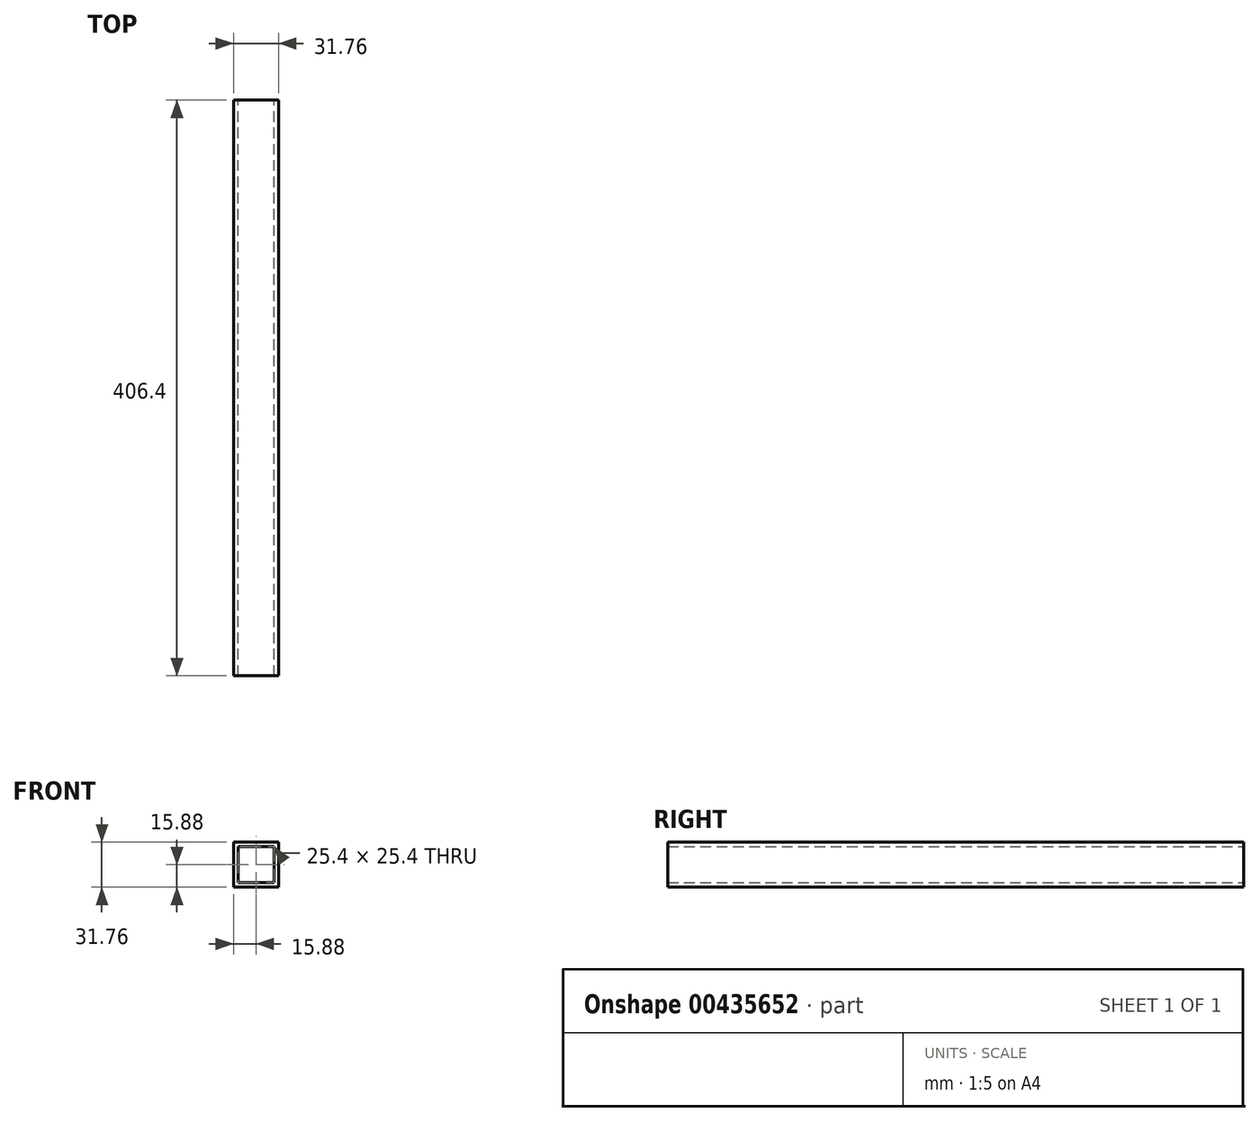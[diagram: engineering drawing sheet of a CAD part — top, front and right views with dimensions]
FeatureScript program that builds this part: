
annotation { "Feature Type Name" : "Feature", "Feature Type Description" : "" }
export const myFeature = defineFeature(function(context is Context, id is Id, definition is map)
    precondition{}
    {
        {
            var Q0;
            Q0=qCreatedBy(makeId("Front.planeOp"),FACE);
            var sketch = newSketch(context, id + "F0", { "sketchPlane" : qUnion([Q0])});
            skLineSegment(sketch, "E0.bottom", {"start": v(12.7, -12.7) * mm, "end": v(-12.7, -12.7) * mm});
            skLineSegment(sketch, "E0.top", {"start": v(12.7, 12.7) * mm, "end": v(-12.7, 12.7) * mm});
            skLineSegment(sketch, "E0.left", {"start": v(12.7, -12.7) * mm, "end": v(12.7, 12.7) * mm});
            skLineSegment(sketch, "E0.right", {"start": v(-12.7, -12.7) * mm, "end": v(-12.7, 12.7) * mm});
            skPoint(sketch, "E0.middle", {"position": v(0, 0) * mm});
            skLineSegment(sketch, "E1.0", {"start": v(15.88, 15.88) * mm, "end": v(-15.87, 15.87) * mm});
            skLineSegment(sketch, "E1.1", {"start": v(15.88, -15.87) * mm, "end": v(15.88, 15.88) * mm});
            skLineSegment(sketch, "E1.2", {"start": v(15.88, -15.87) * mm, "end": v(-15.87, -15.88) * mm});
            skLineSegment(sketch, "E1.3", {"start": v(-15.87, -15.88) * mm, "end": v(-15.87, 15.87) * mm});
            skSolve(sketch);
        }
        {
            var Q0;
            Q0 = qSketchRegion(id + "F0", true);
            extrude(context, id + "F1", {"entities" : qUnion([Q0]), "depth" : 406.4 * mm});
        }
    });
